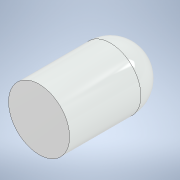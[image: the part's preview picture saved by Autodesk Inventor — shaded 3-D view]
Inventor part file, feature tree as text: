
AUTODESK INVENTOR PART (.ipt)
format: ipt  version: 2021 (Build 250183000, 183)  size: 117,760 bytes
history: native  units: mm
features: extrude x1, fillet x1, sketch x1
ambient origin geometry x8: Origin, YZ Plane, XZ Plane, XY Plane, X Axis, Y Axis, Z Axis, Center Point
bodies: Solid1 (feature_tree)
feature tree (3):
  extrude  "Extrusion1"  Depth=1.5mm TaperAngle=0.0deg
  fillet  "Fillet1"  Radius=1.5mm
  sketch  "Sketch1"  dims[d0=3.0mm d1=5.0mm d2=0.0mm d3=1.5mm]
